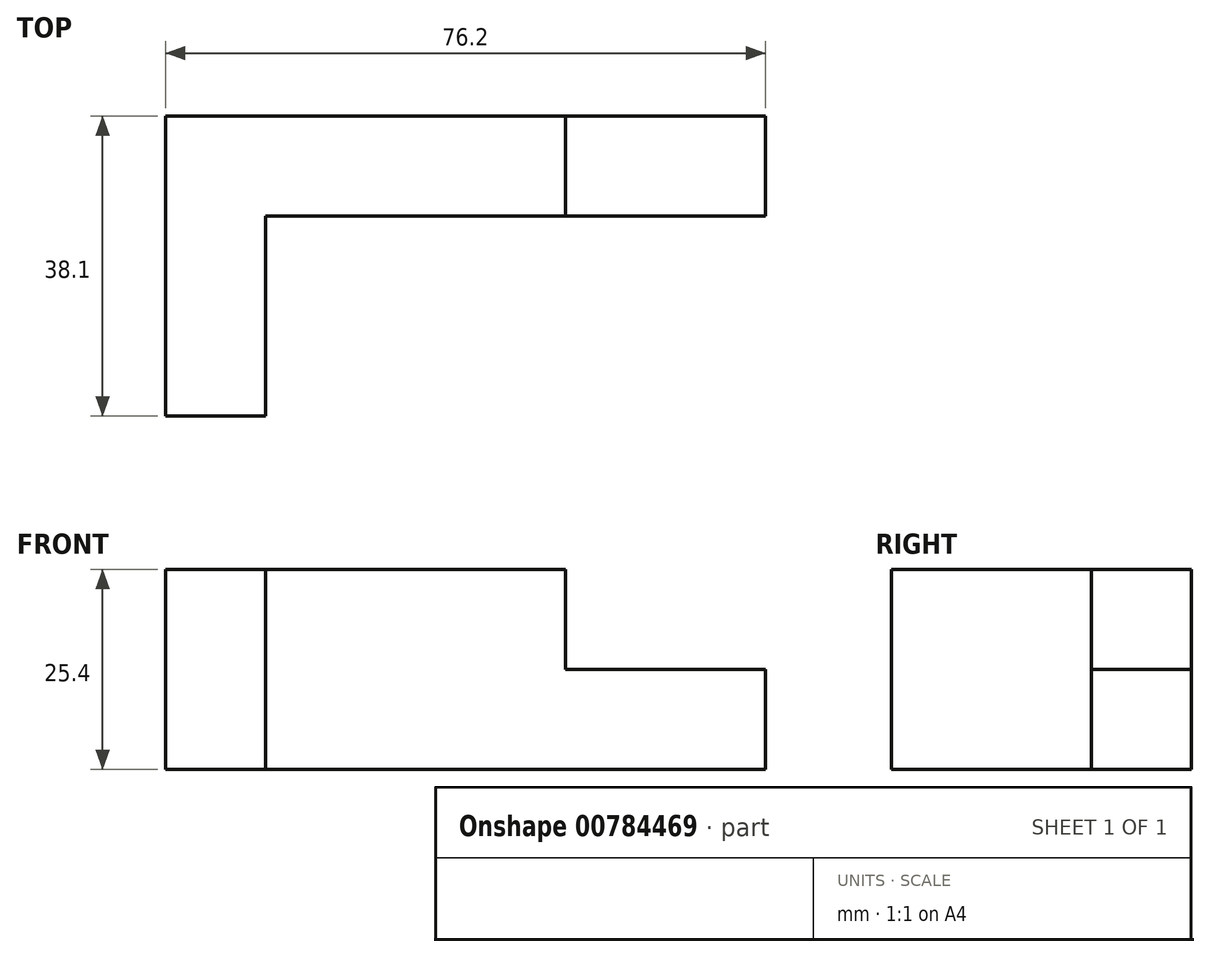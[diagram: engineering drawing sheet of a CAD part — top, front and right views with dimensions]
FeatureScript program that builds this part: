
annotation { "Feature Type Name" : "Feature", "Feature Type Description" : "" }
export const myFeature = defineFeature(function(context is Context, id is Id, definition is map)
    precondition{}
    {
        {
            var Q0;
            Q0=qCreatedBy(makeId("Front.planeOp"),FACE);
            var sketch = newSketch(context, id + "F0", { "sketchPlane" : qUnion([Q0])});
            skLineSegment(sketch, "E0", {"start": v(0, 0) * mm, "end": v(76.2, 0) * mm});
            skLineSegment(sketch, "E1", {"start": v(76.2, 0) * mm, "end": v(76.2, 25.4) * mm});
            skLineSegment(sketch, "E2", {"start": v(76.2, 25.4) * mm, "end": v(0, 25.4) * mm});
            skLineSegment(sketch, "E3", {"start": v(0, 25.4) * mm, "end": v(0, 0) * mm});
            skSolve(sketch);
        }
        {
            var Q0;
            Q0=makeQuery(id+"F0.imprint","IMPRINT",FACE,{"disambiguationData":[TD([[makeQuery(id+"F0.imprint","IMPRINT",EDGE,{"derivedFrom":sQuery(id+"F0.wireOp",EDGE,"E0")}),1.0]])]});
            extrude(context, id + "F1", {"entities" : qUnion([Q0]), "depth" : 38.1 * mm, "offsetDistance" : 25.4 * mm});
        }
        {
            var Q0;
            Q0=makeQuery(id+"F1.opExtrude","SWEPT_FACE",FACE,{"disambiguationData":[OSD([sQuery(id+"F0.wireOp",EDGE,"E1")])]});
            var sketch = newSketch(context, id + "F2", { "sketchPlane" : qUnion([Q0])});
            skLineSegment(sketch, "E4", {"start": v(0, 0) * mm, "end": v(-12.7, 0) * mm});
            skLineSegment(sketch, "E5", {"start": v(-12.7, 0) * mm, "end": v(-12.7, 25.4) * mm});
            skSolve(sketch);
        }
        {
            var Q0;
            {var subQ0=sQuery(id+"F2.wireOp",EDGE,"E5");Q0=makeQuery(id+"F2.imprint","IMPRINT",FACE,{"disambiguationData":[TD([[makeQuery(id+"F2.imprint","IMPRINT",EDGE,{"derivedFrom":subQ0}),1.0]])]});}
            extrude(context, id + "F3", {"entities" : qUnion([Q0]), "operationType" : NewBodyOperationType.REMOVE, "oppositeDirection" : true, "depth" : 63.5 * mm, "offsetDistance" : 25.4 * mm});
        }
        {
            var Q0;
            Q0=makeQuery(id+"F3.boolean.opBoolean","COPY",FACE,{"derivedFrom":makeQuery(id+"F3.opExtrude","SWEPT_FACE",FACE,{"disambiguationData":[OSD([sQuery(id+"F2.wireOp",EDGE,"E5")])]})});
            var sketch = newSketch(context, id + "F4", { "sketchPlane" : qUnion([Q0])});
            skLineSegment(sketch, "E6", {"start": v(12.7, 25.4) * mm, "end": v(41.6, 25.4) * mm});
            skLineSegment(sketch, "E7", {"start": v(12.7, 25.4) * mm, "end": v(50.8, 25.4) * mm});
            skLineSegment(sketch, "E8", {"start": v(76.2, 0) * mm, "end": v(50.8, 0) * mm});
            skLineSegment(sketch, "E9", {"start": v(50.8, 0) * mm, "end": v(50.8, 12.7) * mm});
            skLineSegment(sketch, "E10", {"start": v(50.8, 25.4) * mm, "end": v(50.8, 12.7) * mm});
            skLineSegment(sketch, "E11", {"start": v(50.8, 12.7) * mm, "end": v(76.2, 12.7) * mm});
            skSolve(sketch);
        }
        {
            var Q0;
            {var subQ0=sQuery(id+"F4.wireOp",EDGE,"E10");Q0=makeQuery(id+"F4.imprint","IMPRINT",FACE,{"disambiguationData":[TD([[makeQuery(id+"F4.imprint","IMPRINT",EDGE,{"derivedFrom":subQ0}),1.0]])]});}
            extrude(context, id + "F5", {"entities" : qUnion([Q0]), "operationType" : NewBodyOperationType.REMOVE, "oppositeDirection" : true, "depth" : 12.7 * mm, "offsetDistance" : 25.4 * mm});
        }
    });
